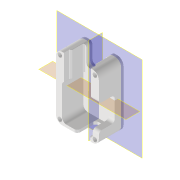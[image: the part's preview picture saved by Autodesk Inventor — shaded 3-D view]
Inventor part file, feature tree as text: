
AUTODESK INVENTOR PART (.ipt)
format: ipt  version: 2022 (Build 260153000, 153)  size: 619,008 bytes
history: native  units: mm
features: reference x25, sketch x14, other x13, extrude x12, projected_geometry x8, plane x5, fillet x5, hole x3, chamfer x1
ambient origin geometry x8: Origin, YZ Plane, XZ Plane, XY Plane, X Axis, Y Axis, Z Axis, Center Point
bodies: Solid1 (feature_tree)
feature tree (86):
  plane  "Work Plane1"
  extrude  "Extrusion1"  Depth=53.8mm
  extrude  "IM_offset"  Depth=53.8mm
  plane  "Arbeitsebene5"
  plane  "Arbeitsebene6"
  extrude  "Extrusion26"  Depth=45.0mm
  chamfer  "Fase2"  Distance=10.0mm
  plane  "Arbeitsebene9"
  extrude  "Extrusion29"  Depth=2.0mm
  extrude  "Extrusion30"  Depth=10.0mm TaperAngle=0.0deg
  plane  "Arbeitsebene10"
  extrude  "Extrusion31"  Depth=2.0mm TaperAngle=45.0deg
  fillet  "Rundung3"  [1 undecoded]
  hole  "Bohrung2"  [1 undecoded]
  extrude  "Extrusion32"  Depth=2.0mm
  hole  "Bohrung3"  [1 undecoded]
  extrude  "Extrusion33"  Depth=10.0mm TaperAngle=0.0deg
  extrude  "Extrusion34"  Depth=2.0mm
  extrude  "Extrusion35"  Depth=2.0mm TaperAngle=0.0deg
  fillet  "Rundung5"  Radius=1.0mm
  hole  "Bohrung4"  [1 undecoded]
  fillet  "Rundung6"  Radius=30.0mm
  extrude  "Extrusion36"  TaperAngle=0.0deg  [1 undecoded]
  fillet  "Rundung7"  Radius=2.0mm
  extrude  "Extrusion37"  Depth=2.0mm
  fillet  "Rundung8"  Radius=7.0mm
  sketch  "Sketch1"  dims[d10=12.0mm d11=0.0mm d18=53.8mm]
  reference  "Reference1"
  reference  "Reference2"
  reference  "Reference3"
  reference  "Reference4"
  reference  "Reference9"
  reference  "Reference20"
  reference  "Reference21"
  reference  "Reference22"
  reference  "Reference23"
  reference  "Reference24"
  sketch  "Skizze4"  dims[d19=45.0deg d20=53.8mm]
  projected_geometry  "Projizierte Kontur1"
  sketch  "Skizze31"  dims[d21=45.0mm d22=45.0mm]
  projected_geometry  "Projizierte Kontur17"
  sketch  "Skizze34"  dims[d30=20.0mm]
  reference  "Referenz35"
  sketch  "Skizze35"  dims[d31=20.0mm]
  reference  "Referenz36"
  reference  "Referenz37"
  reference  "Referenz38"
  reference  "Referenz39"
  reference  "Referenz40"
  sketch  "Skizze37"  dims[d32=2.8mm]
  projected_geometry  "Projizierte Kontur18"
  reference  "Referenz41"
  sketch  "Skizze38"  dims[d33=2.8mm]
  reference  "Referenz42"
  sketch  "Skizze39"  dims[d34=2.8mm]
  reference  "Referenz43"
  sketch  "Skizze40"  dims[d35=3.0mm]
  projected_geometry  "Projizierte Kontur19"
  sketch  "Skizze41"  dims[d36=0.1mm]
  projected_geometry  "Projizierte Kontur20"
  sketch  "Skizze42"  dims[d37=0.1mm]
  projected_geometry  "Projizierte Kontur21"
  projected_geometry  "Projizierte Kontur22"
  sketch  "Skizze43"  dims[d38=0.1mm]
  reference  "Referenz44"
  reference  "Referenz45"
  reference  "Referenz46"
  reference  "Referenz47"
  sketch  "Skizze44"  dims[d39=0.1mm]
  projected_geometry  "Projizierte Kontur23"
  sketch  "Skizze45"  dims[d40=0.2mm d41=10.0mm d42=0.0mm d181=7.5mm d182=10.0mm d183=0.0mm d184=0.5mm d185=2.0mm d186=45.0deg d193=-1.5mm d194=8.6mm d195=8.6mm d196=0.0mm d197=0.0mm d198=10.0mm d199=0.0mm d200=4.0mm d201=12.0mm d202=0.0mm d203=1.0mm d204=30.0mm d205=30.0mm d206=2.8mm d207=6.0mm d208=8.0mm d209=6.0mm d210=90.0deg d211=8.0mm d212=20.594885mm d213=0.0mm d214=0.0mm d215=2.8mm d216=6.0mm d217=4.0mm d218=2.0mm d219=90.0deg d220=8.0mm d221=20.594885mm d222=2.0mm d223=0.0mm d224=1.0mm d225=7.0mm d226=10.0mm d227=0.0mm d229=1.5mm d230=0.0mm d231=2.0mm d232=2.8mm d233=6.0mm d234=4.0mm d235=2.0mm d236=90.0deg d237=8.0mm d238=20.594885mm d239=4.0mm d240=12.0mm d241=24.0mm d242=2.0mm d243=10.0mm d244=0.0mm d245=2.0mm d246=10.0mm d247=0.0mm d248=2.0mm d160=0.5mm d161=0.872665mm d162=0.5mm d163=0.872665mm]
  reference  "Referenz48"
  reference  "Referenz49"
  other  "Assembly_Cube_v2_Thorlabs.iam"
  other  "10_Cube_Base:1"
  other  "00_Base_v0:1"
  other  "Assembly_Cube_Kinematic_Mirrormount_v2.iam"
  other  "Assembly_Cube_empty_1x1_v2:1"
  other  "10_Cube_1x1_v2:1"
  other  "10_Lid_1x1_v2:1"
  other  "Assembly_Cube_SEEED_Xiao_Sense_Camera_adapter_v3.iam"
  other  "00_Seeeduino Xiao:1"
  other  "00_ESP3-CAM:1"
  other  "00_ESP32_XIAO_Adapter_lid:1"
  other  "Baugruppe5"
  other  "10_Cube_Lid:1"
note: 5 required parameter values undecoded (feature->parameter linkage not recoverable at this tier; creation-order binding heuristic only, values carry confidence <= 0.55)
